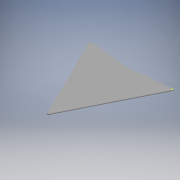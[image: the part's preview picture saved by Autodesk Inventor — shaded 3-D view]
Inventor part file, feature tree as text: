
AUTODESK INVENTOR PART (.ipt)
format: ipt  version: 2018 (Build 220112000, 112)  size: 130,560 bytes
history: native  units: mm
features: sketch x4, extrude x3, projected_geometry x2
ambient origin geometry x8: Origin, YZ Plane, XZ Plane, XY Plane, X Axis, Y Axis, Z Axis, Center Point
bodies: Solid1 (feature_tree)
feature tree (9):
  extrude  "Extrusion1"  Depth=6.0mm TaperAngle=0.0deg
  extrude  "Extrusion2"  Depth=6.0mm
  sketch  "Sketch4"  dims[d6=6.0mm d7=0.0mm]
  extrude  "Extrusion3"  [1 undecoded]
  sketch  "Sketch1"  dims[d0=5.433mm d1=6.0mm d2=0.0mm]
  sketch  "Sketch3"  dims[d3=6.0mm d4=0.0mm d5=11.5mm]
  projected_geometry  "Projected Loop2"
  sketch  "Sketch5"
  projected_geometry  "Projected Loop3"
note: 1 required parameter value undecoded (feature->parameter linkage not recoverable at this tier; creation-order binding heuristic only, values carry confidence <= 0.55)
